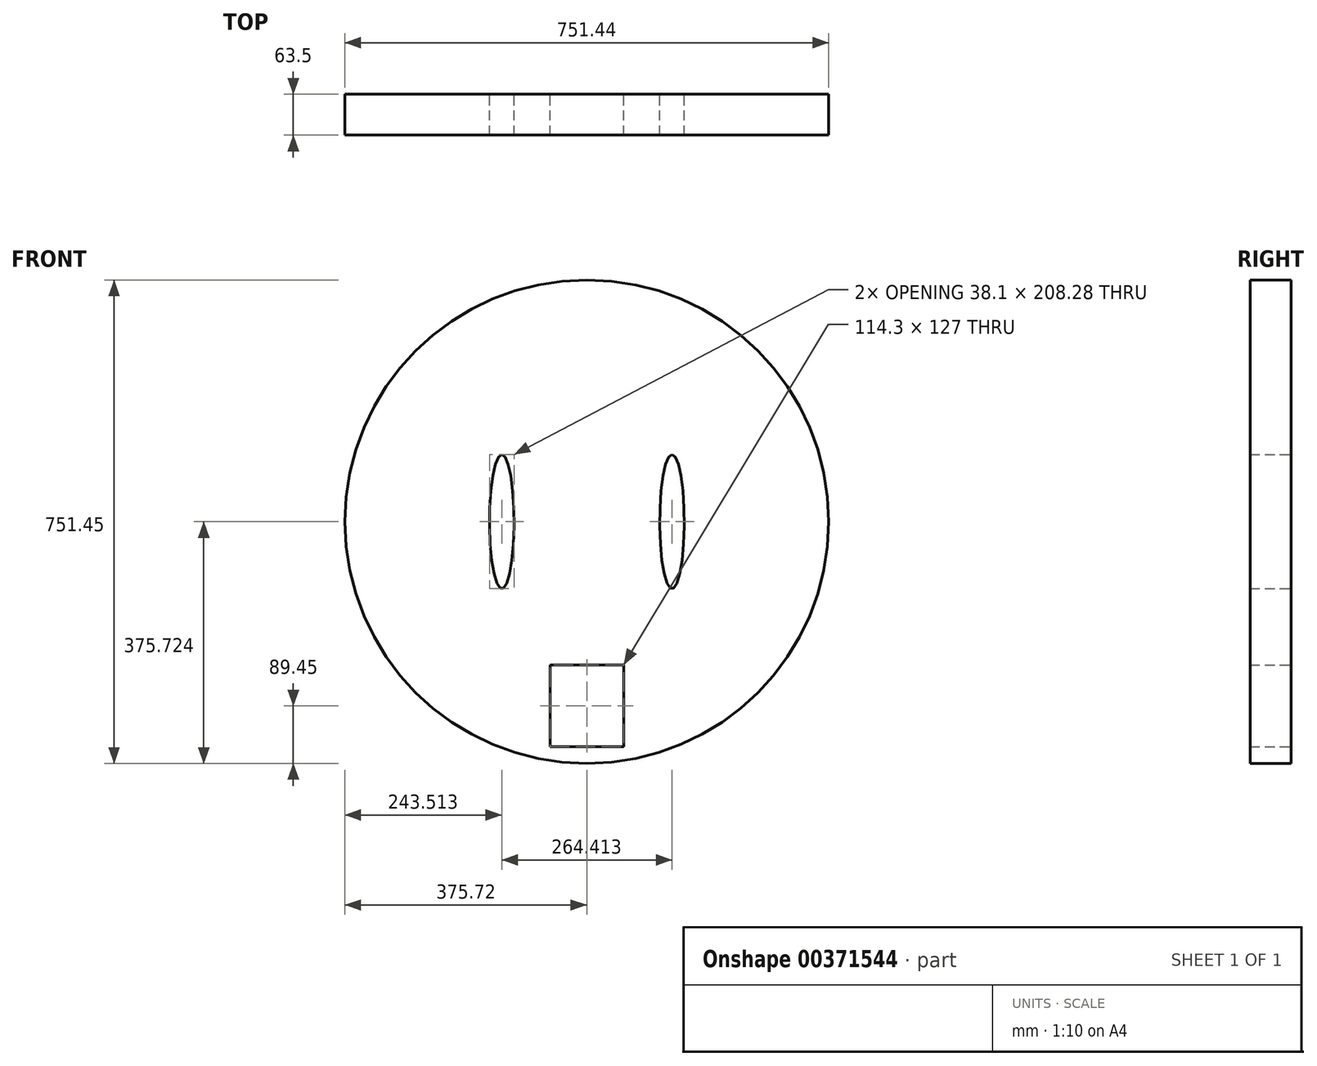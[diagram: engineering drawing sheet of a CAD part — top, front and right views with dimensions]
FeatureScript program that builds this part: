
annotation { "Feature Type Name" : "Feature", "Feature Type Description" : "" }
export const myFeature = defineFeature(function(context is Context, id is Id, definition is map)
    precondition{}
    {
        {
            var Q0;
            Q0=qCreatedBy(makeId("Front.planeOp"),FACE);
            var sketch = newSketch(context, id + "F0", { "sketchPlane" : qUnion([Q0])});
            skCircle(sketch, "E0", {"center": v(0, 360.06) * mm, "radius": 375.72 * mm});
            skEllipse(sketch, "E1", {"center": v(-132.2, 360.06) * mm, "majorRadius": 104.14 * mm, "minorRadius": 19.05 * mm, "majorAxis": v(0, 1)});
            skEllipse(sketch, "E2.MirrorC", {"center": v(132.2, 360.06) * mm, "majorRadius": 104.14 * mm, "minorRadius": 19.05 * mm, "majorAxis": v(0, 1)});
            skLineSegment(sketch, "E3", {"start": v(0, 800.12) * mm, "end": v(0, 0) * mm, "construction": true});
            skLineSegment(sketch, "E4.bottom", {"start": v(57.15, 137.29) * mm, "end": v(-57.15, 137.29) * mm});
            skLineSegment(sketch, "E4.top", {"start": v(57.15, 10.29) * mm, "end": v(-57.15, 10.29) * mm});
            skLineSegment(sketch, "E4.left", {"start": v(57.15, 137.29) * mm, "end": v(57.15, 10.29) * mm});
            skLineSegment(sketch, "E4.right", {"start": v(-57.15, 137.29) * mm, "end": v(-57.15, 10.29) * mm});
            skPoint(sketch, "E4.middle", {"position": v(0, 73.79) * mm});
            skSolve(sketch);
        }
        {
            var Q0;
            Q0=makeQuery(id+"F0.imprint","IMPRINT",FACE,{"disambiguationData":[TD([[makeQuery(id+"F0.imprint","IMPRINT",EDGE,{"derivedFrom":sQuery(id+"F0.wireOp",EDGE,"E1")}),-1.0]])]});
            extrude(context, id + "F1", {"entities" : qUnion([Q0]), "depth" : 63.5 * mm});
        }
    });
